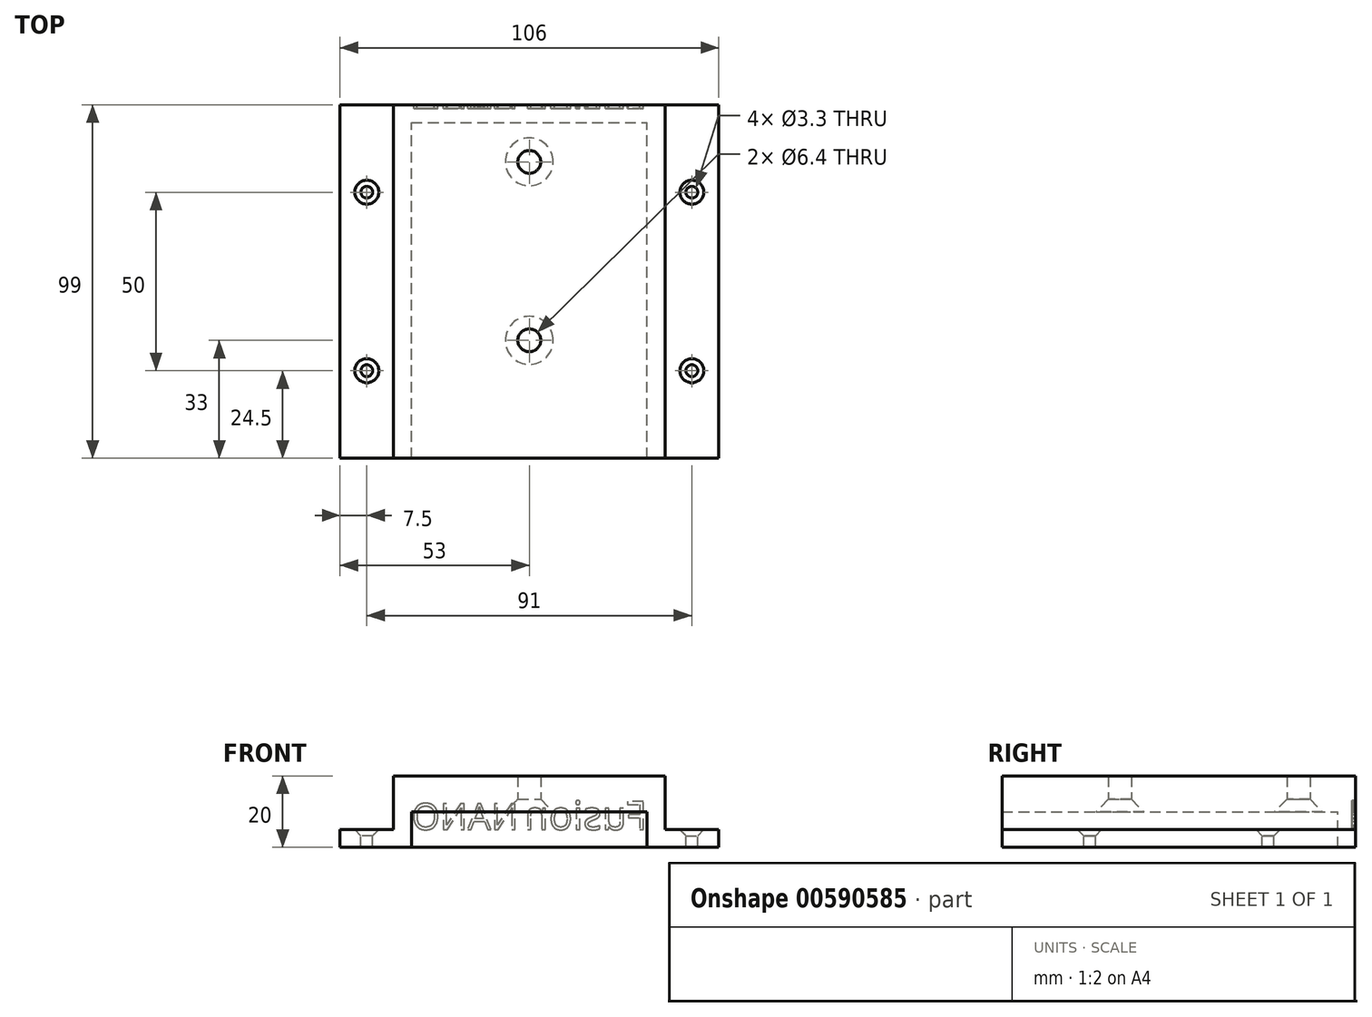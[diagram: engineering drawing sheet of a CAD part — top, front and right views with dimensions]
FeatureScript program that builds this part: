
annotation { "Feature Type Name" : "Feature", "Feature Type Description" : "" }
export const myFeature = defineFeature(function(context is Context, id is Id, definition is map)
    precondition{}
    {
        {
            var Q0;
            Q0=qCreatedBy(makeId("Front.planeOp"),FACE);
            var sketch = newSketch(context, id + "F0", { "sketchPlane" : qUnion([Q0])});
            skLineSegment(sketch, "E0", {"start": v(-53, 5) * mm, "end": v(-38, 5) * mm});
            skLineSegment(sketch, "E1", {"start": v(-38, 5) * mm, "end": v(-38, 20) * mm});
            skLineSegment(sketch, "E2", {"start": v(-38, 20) * mm, "end": v(0, 20) * mm});
            skLineSegment(sketch, "E3", {"start": v(0, 20) * mm, "end": v(0, 10) * mm});
            skLineSegment(sketch, "E4", {"start": v(0, 10) * mm, "end": v(-33, 10) * mm});
            skLineSegment(sketch, "E5", {"start": v(-33, 10) * mm, "end": v(-33, 0) * mm});
            skLineSegment(sketch, "E6", {"start": v(-33, 0) * mm, "end": v(-53, 0) * mm});
            skLineSegment(sketch, "E7", {"start": v(-53, 0) * mm, "end": v(-53, 5) * mm});
            skSolve(sketch);
        }
        {
            var Q0;
            Q0=makeQuery(id+"F0.imprint","IMPRINT",FACE,{"disambiguationData":[TD([[makeQuery(id+"F0.imprint","IMPRINT",EDGE,{"derivedFrom":sQuery(id+"F0.wireOp",EDGE,"E0")}),-1.0]])]});
            extrude(context, id + "F1", {"entities" : qUnion([Q0]), "depth" : 99 * mm, "offsetDistance" : 25 * mm});
        }
        {
            var Q0;
            Q0=makeQuery(id+"F1.opExtrude","SWEPT_FACE",FACE,{"disambiguationData":[OSD([sQuery(id+"F0.wireOp",EDGE,"E0")])]});
            var sketch = newSketch(context, id + "F2", { "sketchPlane" : qUnion([Q0])});
            skLineSegment(sketch, "E8", {"start": v(-45.5, 0) * mm, "end": v(-45.5, -99) * mm, "construction": true});
            skPoint(sketch, "E9", {"position": v(-45.5, -24.5) * mm});
            skPoint(sketch, "E10", {"position": v(-45.5, -74.5) * mm});
            skPoint(sketch, "E11", {"position": v(-45.5, -49.5) * mm});
            skSolve(sketch);
        }
        {
            var Q0;
            Q0=sQuery(id+"F2.wireOp",VERTEX,"E9");
            var Q1;
            Q1=sQuery(id+"F2.wireOp",VERTEX,"E10");
            var Q2;
            Q2=makeQuery(id+"F1.opExtrude","SWEPT_BODY",BODY,{"disambiguationData":[OSD([sQuery(id+"F0.wireOp",EDGE,"E0"),sQuery(id+"F0.wireOp",EDGE,"E1"),sQuery(id+"F0.wireOp",EDGE,"E2"),sQuery(id+"F0.wireOp",EDGE,"E3"),sQuery(id+"F0.wireOp",EDGE,"E4"),sQuery(id+"F0.wireOp",EDGE,"E5"),sQuery(id+"F0.wireOp",EDGE,"E6"),sQuery(id+"F0.wireOp",EDGE,"E7")])]});
            hole(context, id + "F3", {"style" : HoleStyle.C_SINK, "endStyle" : HoleEndStyle.THROUGH, "standardTappedOrClearance" : lookupTablePath({ "standard" : "ISO", "fit" : "Normal", "size" : "M3", "type" : "Clearance" }), "standardBlindInLast" : lookupTablePath({ "fit" : "Standard", "standard" : "ISO", "size" : "M3", "type" : "Clearance" }), "holeDiameter" : 3.3 * mm, "cSinkDiameter" : 6.72 * mm, "cSinkAngle" : 90 * degree, "majorDiameter" : 5 * mm, "isTappedThrough" : true, "tappedDepth" : 12 * mm, "tapClearance" : 3, "locations" : qUnion([Q0, Q1]), "scope" : qUnion([Q2])});
        }
        {
            var Q0;
            Q0=makeQuery(id+"F1.opExtrude","SWEPT_BODY",BODY,{"disambiguationData":[OSD([sQuery(id+"F0.wireOp",EDGE,"E0"),sQuery(id+"F0.wireOp",EDGE,"E1"),sQuery(id+"F0.wireOp",EDGE,"E2"),sQuery(id+"F0.wireOp",EDGE,"E3"),sQuery(id+"F0.wireOp",EDGE,"E4"),sQuery(id+"F0.wireOp",EDGE,"E5"),sQuery(id+"F0.wireOp",EDGE,"E6"),sQuery(id+"F0.wireOp",EDGE,"E7")])]});
            var Q1;
            Q1=qCreatedBy(makeId("Right.planeOp"),FACE);
            mirror(context, id + "F4", {"operationType" : NewBodyOperationType.ADD, "entities" : qUnion([Q0]), "mirrorPlane" : qUnion([Q1])});
        }
        {
            var Q0;
            {var subQ0=makeQuery(id+"F1.opExtrude","SWEPT_FACE",FACE,{"disambiguationData":[OSD([sQuery(id+"F0.wireOp",EDGE,"E4")])]});Q0=makeQuery(id+"F4.boolean.opBoolean","MERGE",FACE,{"derivedFrom":[subQ0,makeQuery(id+"F4.opPattern","COPY",FACE,{"derivedFrom":subQ0,"instanceName":"1"})]});}
            var sketch = newSketch(context, id + "F5", { "sketchPlane" : qUnion([Q0])});
            skLineSegment(sketch, "E12.bottom", {"start": v(-33, 0) * mm, "end": v(33, 0) * mm});
            skLineSegment(sketch, "E12.top", {"start": v(-33, 5) * mm, "end": v(33, 5) * mm});
            skLineSegment(sketch, "E12.left", {"start": v(-33, 0) * mm, "end": v(-33, 5) * mm});
            skLineSegment(sketch, "E12.right", {"start": v(33, 0) * mm, "end": v(33, 5) * mm});
            skSolve(sketch);
        }
        {
            var Q0;
            Q0=qSketchRegion(id+"F5",true);
            var Q1;
            Q1=makeQuery(id+"F4.opPattern","COPY",VERTEX,{"derivedFrom":makeQuery(id+"F1.opExtrude","CAP_VERTEX",VERTEX,{"disambiguationData":[OSD([sQuery(id+"F0.wireOp",EDGE,"E5"),sQuery(id+"F0.wireOp",EDGE,"E6")])],"isStart":true}),"instanceName":"1"});
            extrude(context, id + "F6", {"entities" : qUnion([Q0]), "operationType" : NewBodyOperationType.ADD, "endBound" : BoundingType.UP_TO_VERTEX, "depth" : 25 * mm, "endBoundEntityVertex" : qUnion([Q1]), "offsetDistance" : 25 * mm});
        }
        {
            var Q0;
            {var subQ0=makeQuery(id+"F1.opExtrude","SWEPT_FACE",FACE,{"disambiguationData":[OSD([sQuery(id+"F0.wireOp",EDGE,"E4")])]});Q0=makeQuery(id+"F4.boolean.opBoolean","MERGE",FACE,{"derivedFrom":[subQ0,makeQuery(id+"F4.opPattern","COPY",FACE,{"derivedFrom":subQ0,"instanceName":"1"})]});}
            var sketch = newSketch(context, id + "F7", { "sketchPlane" : qUnion([Q0])});
            skLineSegment(sketch, "E13", {"start": v(0, 99) * mm, "end": v(0, 0) * mm, "construction": true});
            skPoint(sketch, "E13.endSnap0", {"position": v(0, 99) * mm});
            skPoint(sketch, "E14", {"position": v(0, 66) * mm});
            skPoint(sketch, "E15", {"position": v(0, 16) * mm});
            skSolve(sketch);
        }
        {
            var Q0;
            Q0=sQuery(id+"F7.wireOp",VERTEX,"E14");
            var Q1;
            Q1=sQuery(id+"F7.wireOp",VERTEX,"E15");
            var Q2;
            Q2=makeQuery(id+"F1.opExtrude","SWEPT_BODY",BODY,{"disambiguationData":[OSD([sQuery(id+"F0.wireOp",EDGE,"E0"),sQuery(id+"F0.wireOp",EDGE,"E1"),sQuery(id+"F0.wireOp",EDGE,"E2"),sQuery(id+"F0.wireOp",EDGE,"E3"),sQuery(id+"F0.wireOp",EDGE,"E4"),sQuery(id+"F0.wireOp",EDGE,"E5"),sQuery(id+"F0.wireOp",EDGE,"E6"),sQuery(id+"F0.wireOp",EDGE,"E7")])]});
            hole(context, id + "F8", {"style" : HoleStyle.C_SINK, "endStyle" : HoleEndStyle.THROUGH, "standardTappedOrClearance" : lookupTablePath({ "standard" : "ISO", "size" : "6.4", "type" : "Drilled" }), "standardBlindInLast" : lookupTablePath({ "standard" : "ISO", "size" : "6.4", "type" : "Drilled" }), "holeDiameter" : 6.4 * mm, "cSinkDiameter" : 13.44 * mm, "cSinkAngle" : 90 * degree, "majorDiameter" : 6 * mm, "isTappedThrough" : true, "tappedDepth" : 12 * mm, "tapClearance" : 3, "locations" : qUnion([Q0, Q1]), "scope" : qUnion([Q2])});
        }
        {
            var Q0;
            {var subQ0=makeQuery(id+"F1.opExtrude","CAP_FACE",FACE,{"disambiguationData":[OSD([sQuery(id+"F0.wireOp",EDGE,"E0"),sQuery(id+"F0.wireOp",EDGE,"E1"),sQuery(id+"F0.wireOp",EDGE,"E2"),sQuery(id+"F0.wireOp",EDGE,"E3"),sQuery(id+"F0.wireOp",EDGE,"E4"),sQuery(id+"F0.wireOp",EDGE,"E5"),sQuery(id+"F0.wireOp",EDGE,"E6"),sQuery(id+"F0.wireOp",EDGE,"E7")])],"isStart":true});Q0=makeQuery(id+"F6.boolean.opBoolean","MERGE",FACE,{"derivedFrom":[makeQuery(id+"F4.boolean.opBoolean","MERGE",FACE,{"derivedFrom":[subQ0,makeQuery(id+"F4.opPattern","COPY",FACE,{"derivedFrom":subQ0,"instanceName":"1"})]}),makeQuery(id+"F6.opExtrude","SWEPT_FACE",FACE,{"disambiguationData":[OSD([sQuery(id+"F5.wireOp",EDGE,"E12.bottom")])]})]});}
            var sketch = newSketch(context, id + "F9", { "sketchPlane" : qUnion([Q0])});
            skText(sketch, "E16", { "text": "NANO", "fontName": "NotoSans-Regular.ttf"});
            skText(sketch, "E17", { "text": "Fusion", "fontName": "NotoSans-Regular.ttf"});
            const initialGuessF9  = {"E16": [0.003, 0.005, 1, 0, 0.00734], "E17": [-0.033, 0.005, 1, 0, 0.008]};
            skSetInitialGuess(sketch, initialGuessF9);
            skSolve(sketch);
        }
        {
            var Q0;
            Q0=qSketchRegion(id+"F9",true);
            extrude(context, id + "F10", {"entities" : qUnion([Q0]), "operationType" : NewBodyOperationType.REMOVE, "oppositeDirection" : true, "depth" : 1 * mm, "offsetDistance" : 25 * mm});
        }
    });
